# Revit family: RG350PF
name_source: partatom
category: Specialty Equipment
revit_build: Autodesk Revit MEP 2012 (Build: 20110916_2132(x64)
units: mm (PartAtom-declared; Revit-internal decimal feet)

## types (1)
- RG350PF
    Apparent Power = 0 VA
    Assembly Code = E1090320
    Conn Conduit = Yes
    Cycle = 50 Hz
    Depth = 540 mm  [stored 1.77165 ft]
    Description = VEGETABLE PREPARATION MACHINE 12-30 KG/MINUTE WITH MANUAL PUSH FEEDER
    Elec Conn Connection Height = 478 mm  [stored 1.56824 ft]
    FL Amps = 0 A
    Height = 735 mm
    Manufacturer = HALLDE
    Max Overcurrent Protection = 10 A
    Min Ckt Ampacity = 0 A
    Model = RG-350-PF
    Phase = 1
    URL = www.hallde.com
    Volts = 240 V
    Watts = 750 W
    Weight = 32 kg
    Width = 265 mm  [stored 0.869423 ft]

note: [stored X ft] marks values corroborated as IEEE doubles in the binary element streams (Revit-internal decimal feet)

## geometry (parser evidence)
native form markers: Blend x6, Sweep x3
no freeform markers — native parametric forms only
